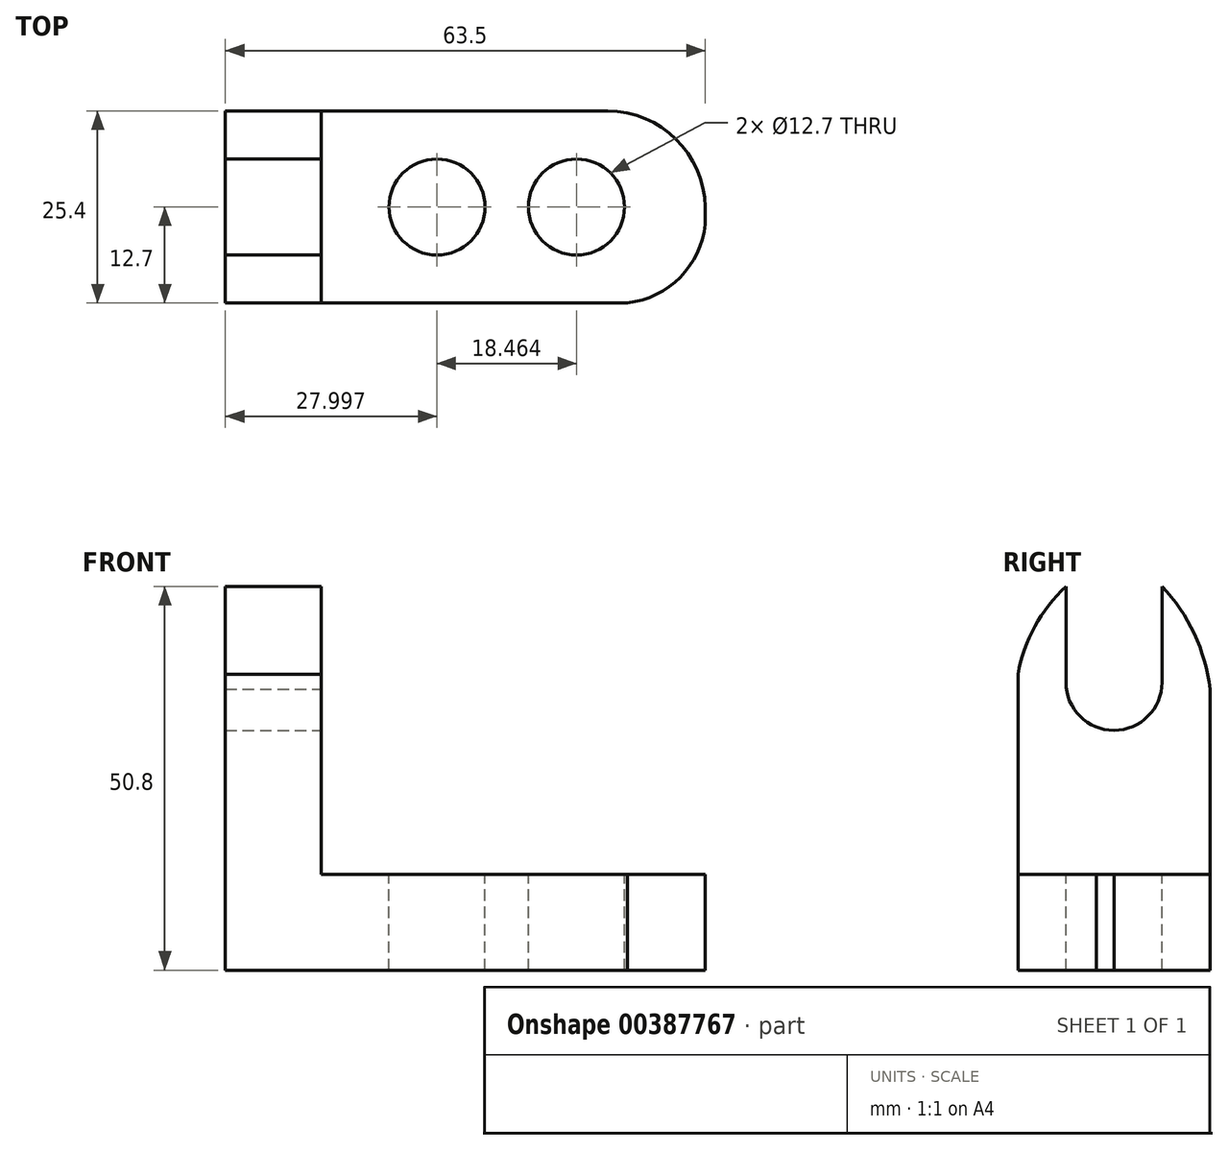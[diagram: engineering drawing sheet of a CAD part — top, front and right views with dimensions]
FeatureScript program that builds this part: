
annotation { "Feature Type Name" : "Feature", "Feature Type Description" : "" }
export const myFeature = defineFeature(function(context is Context, id is Id, definition is map)
    precondition{}
    {
        {
            var Q0;
            Q0=qCreatedBy(makeId("Front.planeOp"),FACE);
            var sketch = newSketch(context, id + "F0", { "sketchPlane" : qUnion([Q0])});
            skLineSegment(sketch, "E0", {"start": v(0, 0) * mm, "end": v(63.5, 0) * mm});
            skLineSegment(sketch, "E1", {"start": v(63.5, 0) * mm, "end": v(63.5, 12.7) * mm});
            skLineSegment(sketch, "E2", {"start": v(63.5, 12.7) * mm, "end": v(12.7, 12.7) * mm});
            skLineSegment(sketch, "E3", {"start": v(12.7, 12.7) * mm, "end": v(12.7, 50.8) * mm});
            skLineSegment(sketch, "E4", {"start": v(12.7, 50.8) * mm, "end": v(0, 50.8) * mm});
            skLineSegment(sketch, "E5", {"start": v(0, 50.8) * mm, "end": v(0, 0) * mm});
            skSolve(sketch);
        }
        {
            var Q0;
            Q0=makeQuery(id+"F0.imprint","IMPRINT",FACE,{"disambiguationData":[TD([[makeQuery(id+"F0.imprint","IMPRINT",EDGE,{"derivedFrom":sQuery(id+"F0.wireOp",EDGE,"E0")}),1.0]])]});
            extrude(context, id + "F1", {"entities" : qUnion([Q0]), "depth" : 25.4 * mm});
        }
        {
            var Q0;
            Q0=makeQuery(id+"F1.opExtrude","SWEPT_FACE",FACE,{"disambiguationData":[OSD([sQuery(id+"F0.wireOp",EDGE,"E2")])]});
            var sketch = newSketch(context, id + "F2", { "sketchPlane" : qUnion([Q0])});
            skCircle(sketch, "E6", {"center": v(28, -12.7) * mm, "radius": 6.35 * mm});
            skCircle(sketch, "E7", {"center": v(46.46, -12.7) * mm, "radius": 6.35 * mm});
            skSolve(sketch);
        }
        {
            var Q0;
            Q0=makeQuery(id+"F2.imprint","IMPRINT",FACE,{"disambiguationData":[TD([[makeQuery(id+"F2.imprint","IMPRINT",EDGE,{"derivedFrom":sQuery(id+"F2.wireOp",EDGE,"E6")}),1.0]])]});
            var Q1;
            Q1=makeQuery(id+"F2.imprint","IMPRINT",FACE,{"disambiguationData":[TD([[makeQuery(id+"F2.imprint","IMPRINT",EDGE,{"derivedFrom":sQuery(id+"F2.wireOp",EDGE,"E7")}),1.0]])]});
            extrude(context, id + "F3", {"entities" : qUnion([Q0, Q1]), "operationType" : NewBodyOperationType.REMOVE, "oppositeDirection" : true, "depth" : 25.4 * mm});
        }
        {
            var Q0;
            Q0=makeQuery(id+"F1.opExtrude","SWEPT_FACE",FACE,{"disambiguationData":[OSD([sQuery(id+"F0.wireOp",EDGE,"E2")])]});
            var sketch = newSketch(context, id + "F4", { "sketchPlane" : qUnion([Q0])});
            skArc(sketch, "E8", {"start": v(50.45, -25.4) * mm, "mid": v(59.14, -22.93) * mm, "end": v(63.5, -15.01) * mm});
            skArc(sketch, "E9", {"start": v(63.5, -12.7) * mm, "mid": v(59.58, -3.68) * mm, "end": v(50.45, 0) * mm});
            skSolve(sketch);
        }
        {
            var Q0;
            Q0 = qSketchRegion(id + "F4", true);
            var Q1;
            {var subQ0=sQuery(id+"F4.wireOp",EDGE,"E9");var subQ1=sQuery(id+"F0.wireOp",EDGE,"E2");var subQ4=makeQuery(id+"F1.opExtrude","CAP_EDGE",EDGE,{"disambiguationData":[OSD([subQ1])],"isStart":true});var subQ5=makeQuery(id+"F4.imprint","INTERSECT",VERTEX,{"disambiguationData":[OD(1.0)],"derivedFrom":[subQ4,subQ0]});Q1=makeQuery(id+"F4.imprint","IMPRINT",FACE,{"disambiguationData":[TD([[makeQuery(id+"F4.imprint","IMPRINT",EDGE,{"disambiguationData":[TD([[subQ5,1.0]])],"derivedFrom":subQ0}),-1.0]])]});}
            var Q2;
            {var subQ0=sQuery(id+"F4.wireOp",EDGE,"E8");var subQ1=sQuery(id+"F0.wireOp",EDGE,"E2");var subQ4=makeQuery(id+"F1.opExtrude","CAP_EDGE",EDGE,{"disambiguationData":[OSD([subQ1])],"isStart":false});var subQ5=makeQuery(id+"F4.imprint","INTERSECT",VERTEX,{"disambiguationData":[OD(1.0)],"derivedFrom":[subQ4,subQ0]});Q2=makeQuery(id+"F4.imprint","IMPRINT",FACE,{"disambiguationData":[TD([[makeQuery(id+"F4.imprint","IMPRINT",EDGE,{"disambiguationData":[TD([[subQ5,-1.0]])],"derivedFrom":subQ0}),-1.0]])]});}
            extrude(context, id + "F5", {"entities" : qUnion([Q0, Q1, Q2]), "operationType" : NewBodyOperationType.REMOVE, "oppositeDirection" : true, "depth" : 25.4 * mm});
        }
        {
            var Q0;
            Q0=makeQuery(id+"F1.opExtrude","SWEPT_FACE",FACE,{"disambiguationData":[OSD([sQuery(id+"F0.wireOp",EDGE,"E3")])]});
            var sketch = newSketch(context, id + "F6", { "sketchPlane" : qUnion([Q0])});
            skCircle(sketch, "E10", {"center": v(-12.7, 38.1) * mm, "radius": 6.35 * mm});
            skLineSegment(sketch, "E11", {"start": v(-6.35, 38.1) * mm, "end": v(-6.35, 50.8) * mm});
            skLineSegment(sketch, "E12", {"start": v(-19.05, 38.1) * mm, "end": v(-19.05, 50.8) * mm});
            skSolve(sketch);
        }
        {
            var Q0;
            {var subQ0=sQuery(id+"F6.wireOp",EDGE,"E11");Q0=makeQuery(id+"F6.imprint","IMPRINT",FACE,{"disambiguationData":[TD([[makeQuery(id+"F6.imprint","IMPRINT",EDGE,{"derivedFrom":subQ0}),1.0]])]});}
            var Q1;
            {var subQ0=sQuery(id+"F6.wireOp",EDGE,"E10");var subQ1=makeQuery(id+"F6.imprint","INTERSECT",VERTEX,{"derivedFrom":[subQ0,sQuery(id+"F6.wireOp",EDGE,"E11")]});Q1=makeQuery(id+"F6.imprint","IMPRINT",FACE,{"disambiguationData":[TD([[makeQuery(id+"F6.imprint","IMPRINT",EDGE,{"disambiguationData":[TD([[subQ1,-1.0]])],"derivedFrom":subQ0}),1.0]])]});}
            extrude(context, id + "F7", {"entities" : qUnion([Q0, Q1]), "operationType" : NewBodyOperationType.REMOVE, "oppositeDirection" : true, "depth" : 25.4 * mm});
        }
        {
            var Q0;
            Q0=makeQuery(id+"F1.opExtrude","SWEPT_FACE",FACE,{"disambiguationData":[OSD([sQuery(id+"F0.wireOp",EDGE,"E3")])]});
            var sketch = newSketch(context, id + "F8", { "sketchPlane" : qUnion([Q0])});
            skArc(sketch, "E13", {"start": v(-19.05, 50.8) * mm, "mid": v(-24.65, 42.08) * mm, "end": v(-25.4, 31.75) * mm});
            skArc(sketch, "E14", {"start": v(0, 31.75) * mm, "mid": v(-1.06, 41.98) * mm, "end": v(-6.35, 50.8) * mm});
            skSolve(sketch);
        }
        {
            var Q0;
            Q0 = qSketchRegion(id + "F8", true);
            var Q1;
            {var subQ1=sQuery(id+"F0.wireOp",EDGE,"E4");var subQ2=sQuery(id+"F0.wireOp",EDGE,"E3");var subQ3=sQuery(id+"F6.wireOp",EDGE,"E12");var subQ4=makeQuery(id+"F7.boolean.opBoolean","SPLIT",EDGE,{"disambiguationData":[TD([makeQuery(id+"F7.opExtrude","SWEPT_FACE",FACE,{"disambiguationData":[OSD([subQ3])]})])],"derivedFrom":makeQuery(id+"F1.opExtrude","SWEPT_EDGE",EDGE,{"disambiguationData":[OSD([subQ2,subQ1])]})});Q1=makeQuery(id+"F8.imprint","IMPRINT",FACE,{"disambiguationData":[TD([[makeQuery(id+"F8.imprint","IMPRINT",EDGE,{"derivedFrom":subQ4}),-1.0]])]});}
            var Q2;
            {var subQ1=sQuery(id+"F0.wireOp",EDGE,"E4");var subQ2=sQuery(id+"F0.wireOp",EDGE,"E3");var subQ3=sQuery(id+"F6.wireOp",EDGE,"E11");var subQ4=makeQuery(id+"F7.boolean.opBoolean","SPLIT",EDGE,{"disambiguationData":[TD([makeQuery(id+"F7.opExtrude","SWEPT_FACE",FACE,{"disambiguationData":[OSD([subQ3])]})])],"derivedFrom":makeQuery(id+"F1.opExtrude","SWEPT_EDGE",EDGE,{"disambiguationData":[OSD([subQ2,subQ1])]})});Q2=makeQuery(id+"F8.imprint","IMPRINT",FACE,{"disambiguationData":[TD([[makeQuery(id+"F8.imprint","IMPRINT",EDGE,{"derivedFrom":subQ4}),-1.0]])]});}
            extrude(context, id + "F9", {"entities" : qUnion([Q0, Q1, Q2]), "operationType" : NewBodyOperationType.REMOVE, "oppositeDirection" : true, "depth" : 25.4 * mm});
        }
    });
